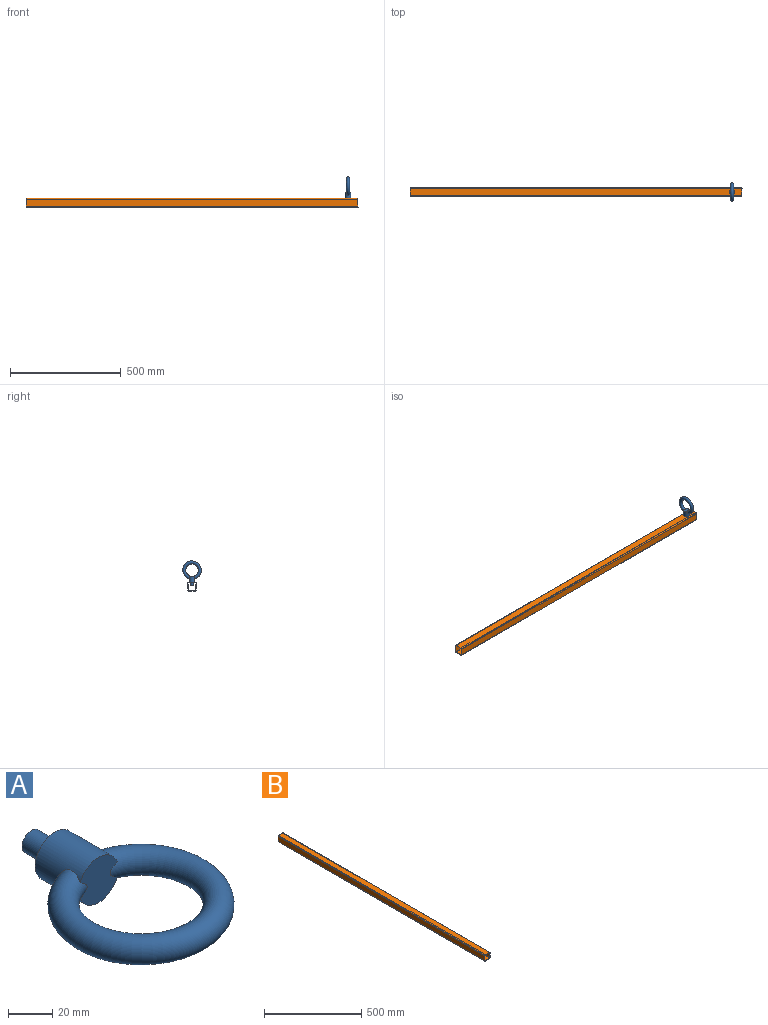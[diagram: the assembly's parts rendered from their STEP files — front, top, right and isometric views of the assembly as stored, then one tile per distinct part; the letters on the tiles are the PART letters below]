
ASSEMBLY  parts=2 mates=1
PART A: 6 faces, bbox 90.9x115.5x25 mm
  f0: cylinder r=12.5mm len=28mm, axis (0,-1,0), area 1878.7mm2, adj f1,f2,f5
  f1: plane 25x25mm, normal (0,1,0), area 381.5mm2, adj f0,f3
  f2: plane 25x23.51mm, normal (0,-1,0), area 434mm2, adj f0,f5
  f3: cylinder r=5.9mm len=15mm, axis (0,-1,0), area 556.1mm2, adj f1,f4
  f4: plane 11.8x11.8mm, normal (0,1,0), area 109.4mm2, adj f3
  f5: torus R=35mm, axis (0,0,1), area 8707.9mm2, adj f0,f2
PART B: 15 faces, bbox 40x1500x40 mm
  f0: plane 1500x30mm, normal (0,0,-1), area 44877.3mm2, adj f8,f9,f10,f13,f14
  f1: plane 1500x30mm, normal (1,0,0), area 45000mm2, adj f8,f9,f10,f11
  f2: plane 1500x30mm, normal (0,0,1), area 45000mm2, adj f8,f9,f11,f12
  f3: plane 1500x34mm, normal (-1,0,0), area 51000mm2, adj f4,f6,f8,f9
  f4: plane 1500x34mm, normal (0,0,1), area 50877.3mm2, adj f3,f5,f8,f9,f14
  f5: plane 1500x34mm, normal (1,0,0), area 51000mm2, adj f4,f6,f8,f9
  f6: plane 1500x34mm, normal (0,0,-1), area 51000mm2, adj f3,f5,f8,f9
  f7: plane 1500x30mm, normal (-1,0,0), area 45000mm2, adj f8,f9,f12,f13
  f8: plane 40x40mm, normal (0,-1,0), area 422.5mm2, adj f0,f1,f2,f3,f4,f5,f6,f7
  f9: plane 40x40mm, normal (0,1,0), area 422.5mm2, adj f0,f1,f2,f3,f4,f5,f6,f7
  f10: cylinder r=5mm len=1500mm, axis (0,-1,0), area 11781mm2, adj f0,f1,f8,f9
  f11: cylinder r=5mm len=1500mm, axis (0,1,0), area 11781mm2, adj f1,f2,f8,f9
  f12: cylinder r=5mm len=1500mm, axis (0,-1,0), area 11781mm2, adj f2,f7,f8,f9
  f13: cylinder r=5mm len=1500mm, axis (0,1,0), area 11781mm2, adj f0,f7,f8,f9
  f14: cylinder r=6.25mm len=12.5mm, axis (0,0,-1), area 117.8mm2, adj f0,f4
PLACE A rot(axis=(-0.58,-0.58,0.58),120deg) t=(-480.21,-308.32,-298.33)mm
PLACE B rot(axis=(-0.71,0.71,0),180deg) t=(-1935.21,-308.32,-373.33)mm fixed
MATE fastened A.f0 <-> B.f14  axis (0,0,-1) through (-480.21,-308.32,-353.33)mm
